# Revit family: Sanitary_Taps-Mixers_hansgrohe_76074CHN-Finoris-Single-lever-basin-mixe_NEW
name_source: partatom
category: Plumbing Fixtures
revit_build: Autodesk Revit 2015 (Build: 20140903_1530(x64)
units: mm (PartAtom-declared; Revit-internal decimal feet)

## types (1)
- 007 Chrome
    Always visible = Yes
    BIMobject category = Taps & Mixers
    BIMobject category code = sanitary-taps-mixers
    BIMobject main category = Sanitary
    BIMobject main category code = sanitary
    Brand url = http://www.hansgrohe-int.com
    Design country = Germany
    Edition number = 1
    GTIN code = https://4059625356432
    IFC Classification = Sanitary Terminal
    Installation instructions = https://www.hansgrohe.com
    Manufacturer country = Germany
    Manufacturer name = hansgrohe
    Material 1 = Hansgrohe - Finoris - 007 Chrome
    Material main = Chrome
    Material secondary = Chrome
    Product Guid = fdbdb116-42c7-45c0-8929-cab305bb8741
    Product SKU = 76074CHN
    Product data url = https://bimobject.com
    Product family = Finoris
    Product group = Basin mixers
    Product name = 76074CHN Finoris Single lever basin mixer 260 for washbowls with waste set
    Product url = https://www.hansgrohe.com
    QR code = http://bimobject.com
    Technical description = https://www.hansgrohe.com

## geometry (parser evidence)
native form markers: Sweep x2
no freeform markers — native parametric forms only
